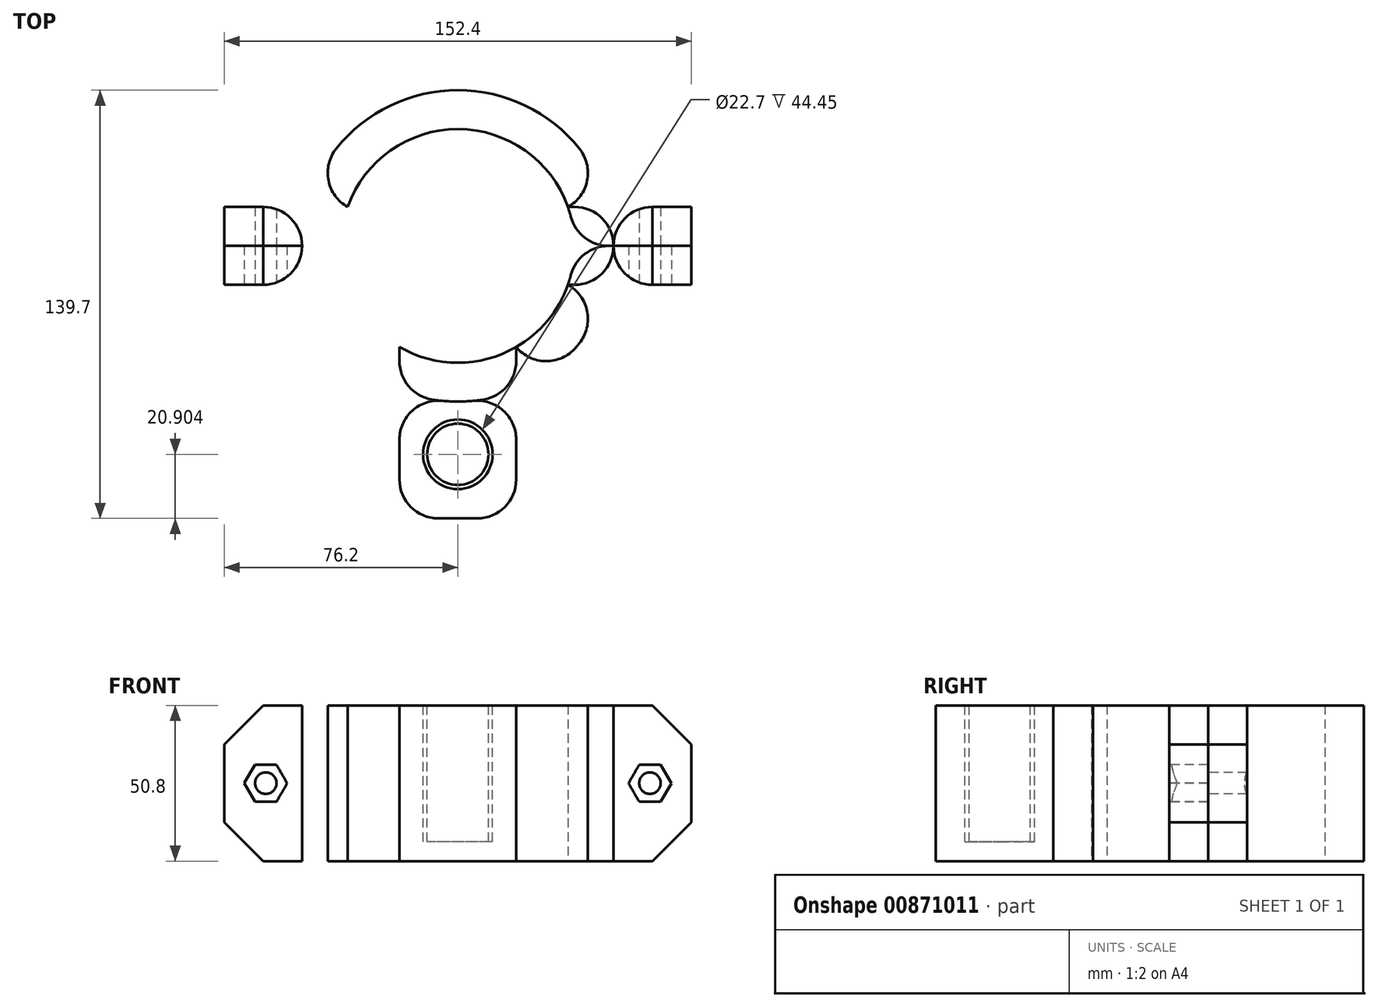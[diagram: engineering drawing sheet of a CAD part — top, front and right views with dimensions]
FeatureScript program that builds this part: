
annotation { "Feature Type Name" : "Feature", "Feature Type Description" : "" }
export const myFeature = defineFeature(function(context is Context, id is Id, definition is map)
    precondition{}
    {
        {
            var Q0;
            Q0=qCreatedBy(makeId("Top.planeOp"),FACE);
            var sketch = newSketch(context, id + "F0", { "sketchPlane" : qUnion([Q0])});
            skCircle(sketch, "E0", {"center": v(0, 0) * mm, "radius": 38.1 * mm});
            skCircle(sketch, "E1", {"center": v(0, 0) * mm, "radius": 50.8 * mm});
            skLineSegment(sketch, "E2.bottom", {"start": v(76.2, -12.7) * mm, "end": v(-76.2, -12.7) * mm});
            skLineSegment(sketch, "E2.top", {"start": v(76.2, 12.7) * mm, "end": v(-76.2, 12.7) * mm});
            skLineSegment(sketch, "E2.left", {"start": v(76.2, -12.7) * mm, "end": v(76.2, 12.7) * mm});
            skLineSegment(sketch, "E2.right", {"start": v(-76.2, -12.7) * mm, "end": v(-76.2, 12.7) * mm});
            skPoint(sketch, "E3", {"position": v(0, -50.8) * mm});
            skLineSegment(sketch, "E4.bottom", {"start": v(19.05, -12.7) * mm, "end": v(-19.05, -12.7) * mm});
            skLineSegment(sketch, "E4.top", {"start": v(19.05, -88.9) * mm, "end": v(-19.05, -88.9) * mm});
            skLineSegment(sketch, "E4.left", {"start": v(19.05, -12.7) * mm, "end": v(19.05, -88.9) * mm});
            skLineSegment(sketch, "E4.right", {"start": v(-19.05, -12.7) * mm, "end": v(-19.05, -88.9) * mm});
            skSolve(sketch);
        }
        {
            var Q0;
            {var subQ0=sQuery(id+"F0.wireOp",EDGE,"E2.top");var subQ1=sQuery(id+"F0.wireOp",EDGE,"E0");var subQ2=makeQuery(id+"F0.imprint","INTERSECT",VERTEX,{"disambiguationData":[OD(0.0)],"derivedFrom":[subQ1,subQ0]});Q0=makeQuery(id+"F0.imprint","IMPRINT",FACE,{"disambiguationData":[TD([[makeQuery(id+"F0.imprint","IMPRINT",EDGE,{"disambiguationData":[TD([[subQ2,1.0]])],"derivedFrom":subQ1}),-1.0]])]});}
            var Q1;
            {var subQ5=sQuery(id+"F0.wireOp",EDGE,"E2.right");Q1=makeQuery(id+"F0.imprint","IMPRINT",FACE,{"disambiguationData":[TD([[makeQuery(id+"F0.imprint","IMPRINT",EDGE,{"derivedFrom":subQ5}),-1.0]])]});}
            var Q2;
            {var subQ0=sQuery(id+"F0.wireOp",EDGE,"E2.top");var subQ1=sQuery(id+"F0.wireOp",EDGE,"E0");var subQ2=makeQuery(id+"F0.imprint","INTERSECT",VERTEX,{"disambiguationData":[OD(0.0)],"derivedFrom":[subQ1,subQ0]});Q2=makeQuery(id+"F0.imprint","IMPRINT",FACE,{"disambiguationData":[TD([[makeQuery(id+"F0.imprint","IMPRINT",EDGE,{"disambiguationData":[TD([[subQ2,-1.0]])],"derivedFrom":subQ1}),-1.0]])]});}
            var Q3;
            {var subQ0=sQuery(id+"F0.wireOp",EDGE,"E2.top");var subQ1=sQuery(id+"F0.wireOp",EDGE,"E0");var subQ2=makeQuery(id+"F0.imprint","INTERSECT",VERTEX,{"disambiguationData":[OD(1.0)],"derivedFrom":[subQ1,subQ0]});Q3=makeQuery(id+"F0.imprint","IMPRINT",FACE,{"disambiguationData":[TD([[makeQuery(id+"F0.imprint","IMPRINT",EDGE,{"disambiguationData":[TD([[subQ2,1.0]])],"derivedFrom":subQ1}),-1.0]])]});}
            var Q4;
            {var subQ5=sQuery(id+"F0.wireOp",EDGE,"E2.left");Q4=makeQuery(id+"F0.imprint","IMPRINT",FACE,{"disambiguationData":[TD([[makeQuery(id+"F0.imprint","IMPRINT",EDGE,{"derivedFrom":subQ5}),1.0]])]});}
            var Q5;
            {var subQ0=sQuery(id+"F0.wireOp",EDGE,"E2.bottom");var subQ1=sQuery(id+"F0.wireOp",EDGE,"E0");var subQ2=makeQuery(id+"F0.imprint","INTERSECT",VERTEX,{"disambiguationData":[OD(0.0)],"derivedFrom":[subQ1,subQ0]});Q5=makeQuery(id+"F0.imprint","IMPRINT",FACE,{"disambiguationData":[TD([[makeQuery(id+"F0.imprint","IMPRINT",EDGE,{"disambiguationData":[TD([[subQ2,-1.0]])],"derivedFrom":subQ1}),-1.0]])]});}
            var Q6;
            {var subQ0=sQuery(id+"F0.wireOp",EDGE,"E4.left");var subQ1=sQuery(id+"F0.wireOp",EDGE,"E0");var subQ2=makeQuery(id+"F0.imprint","INTERSECT",VERTEX,{"derivedFrom":[subQ1,subQ0]});Q6=makeQuery(id+"F0.imprint","IMPRINT",FACE,{"disambiguationData":[TD([[makeQuery(id+"F0.imprint","IMPRINT",EDGE,{"disambiguationData":[TD([[subQ2,-1.0]])],"derivedFrom":subQ1}),-1.0]])]});}
            var Q7;
            {var subQ0=sQuery(id+"F0.wireOp",EDGE,"E4.right");var subQ1=sQuery(id+"F0.wireOp",EDGE,"E0");var subQ2=makeQuery(id+"F0.imprint","INTERSECT",VERTEX,{"derivedFrom":[subQ1,subQ0]});Q7=makeQuery(id+"F0.imprint","IMPRINT",FACE,{"disambiguationData":[TD([[makeQuery(id+"F0.imprint","IMPRINT",EDGE,{"disambiguationData":[TD([[subQ2,-1.0]])],"derivedFrom":subQ1}),-1.0]])]});}
            var Q8;
            {var subQ5=sQuery(id+"F0.wireOp",EDGE,"E4.top");Q8=makeQuery(id+"F0.imprint","IMPRINT",FACE,{"disambiguationData":[TD([[makeQuery(id+"F0.imprint","IMPRINT",EDGE,{"derivedFrom":subQ5}),-1.0]])]});}
            extrude(context, id + "F1", {"entities" : qUnion([Q0, Q1, Q2, Q3, Q4, Q5, Q6, Q7, Q8]), "depth" : 50.8 * mm, "offsetDistance" : 25 * mm});
        }
        {
            var Q0;
            {var subQ0=sQuery(id+"F0.wireOp",EDGE,"E2.bottom");Q0=makeQuery(id+"F1.opExtrude","SWEPT_FACE",FACE,{"disambiguationData":[OSD([subQ0]),TDD([makeQuery(id+"F0.imprint","IMPRINT",EDGE,{"disambiguationData":[TD([[makeQuery(id+"F0.imprint","INTERSECT",VERTEX,{"derivedFrom":[subQ0,sQuery(id+"F0.wireOp",EDGE,"E2.right")]}),1.0]])],"derivedFrom":subQ0})])]});}
            var sketch = newSketch(context, id + "F2", { "sketchPlane" : qUnion([Q0])});
            skPoint(sketch, "E5", {"position": v(-62.7, 25.4) * mm});
            skPoint(sketch, "E5.positionSnap0", {"position": v(-76.2, 25.4) * mm});
            skPoint(sketch, "E5.positionSnap1", {"position": v(-62.7, 50.8) * mm});
            skPoint(sketch, "E6", {"position": v(62.7, 25.4) * mm});
            skCircle(sketch, "E7.cCircle", {"center": v(-62.7, 25.4) * mm, "radius": 7 * mm, "construction": true});
            skLineSegment(sketch, "E7.0", {"start": v(-59.16, 31.44) * mm, "end": v(-55.7, 25.36) * mm});
            skLineSegment(sketch, "E7.1", {"start": v(-55.7, 25.36) * mm, "end": v(-59.23, 19.32) * mm});
            skLineSegment(sketch, "E7.2", {"start": v(-59.23, 19.32) * mm, "end": v(-66.23, 19.36) * mm});
            skLineSegment(sketch, "E7.3", {"start": v(-66.23, 19.36) * mm, "end": v(-69.7, 25.44) * mm});
            skLineSegment(sketch, "E7.4", {"start": v(-69.7, 25.44) * mm, "end": v(-66.16, 31.48) * mm});
            skLineSegment(sketch, "E7.5", {"start": v(-66.16, 31.48) * mm, "end": v(-59.16, 31.44) * mm});
            skCircle(sketch, "E8.cCircle", {"center": v(62.7, 25.4) * mm, "radius": 7 * mm, "construction": true});
            skLineSegment(sketch, "E8.0", {"start": v(55.7, 25.4) * mm, "end": v(59.2, 31.46) * mm});
            skLineSegment(sketch, "E8.1", {"start": v(59.2, 31.46) * mm, "end": v(66.2, 31.46) * mm});
            skLineSegment(sketch, "E8.2", {"start": v(66.2, 31.46) * mm, "end": v(69.7, 25.4) * mm});
            skLineSegment(sketch, "E8.3", {"start": v(69.7, 25.4) * mm, "end": v(66.2, 19.34) * mm});
            skLineSegment(sketch, "E8.4", {"start": v(66.2, 19.34) * mm, "end": v(59.2, 19.34) * mm});
            skLineSegment(sketch, "E8.5", {"start": v(59.2, 19.34) * mm, "end": v(55.7, 25.4) * mm});
            skSolve(sketch);
        }
        {
            var Q0;
            Q0 = qSketchRegion(id + "F2", true);
            extrude(context, id + "F3", {"entities" : qUnion([Q0]), "operationType" : NewBodyOperationType.REMOVE, "oppositeDirection" : true, "depth" : 12.7 * mm, "offsetDistance" : 25 * mm});
        }
        {
            var Q0;
            Q0=makeQuery(id+"F1.opExtrude","CAP_EDGE",EDGE,{"disambiguationData":[OSD([sQuery(id+"F0.wireOp",EDGE,"E2.right")])],"isStart":false});
            var Q1;
            Q1=makeQuery(id+"F1.opExtrude","CAP_EDGE",EDGE,{"disambiguationData":[OSD([sQuery(id+"F0.wireOp",EDGE,"E2.right")])],"isStart":true});
            var Q2;
            Q2=makeQuery(id+"F1.opExtrude","CAP_EDGE",EDGE,{"disambiguationData":[OSD([sQuery(id+"F0.wireOp",EDGE,"E2.left")])],"isStart":false});
            var Q3;
            Q3=makeQuery(id+"F1.opExtrude","CAP_EDGE",EDGE,{"disambiguationData":[OSD([sQuery(id+"F0.wireOp",EDGE,"E2.left")])],"isStart":true});
            chamfer(context, id + "F4", {"entities" : qUnion([Q0, Q1, Q2, Q3]), "width" : 12.7 * mm, "tangentPropagation" : true});
        }
        {
            var Q0;
            Q0=makeQuery(id+"F1.opExtrude","CAP_FACE",FACE,{"disambiguationData":[OSD([sQuery(id+"F0.wireOp",EDGE,"E0"),sQuery(id+"F0.wireOp",EDGE,"E1"),sQuery(id+"F0.wireOp",EDGE,"E2.bottom"),sQuery(id+"F0.wireOp",EDGE,"E2.top"),sQuery(id+"F0.wireOp",EDGE,"E2.left"),sQuery(id+"F0.wireOp",EDGE,"E2.right"),sQuery(id+"F0.wireOp",EDGE,"E4.top"),sQuery(id+"F0.wireOp",EDGE,"E4.left"),sQuery(id+"F0.wireOp",EDGE,"E4.right")])],"isStart":false});
            var sketch = newSketch(context, id + "F5", { "sketchPlane" : qUnion([Q0])});
            skPoint(sketch, "E9", {"position": v(0, -68) * mm});
            skPoint(sketch, "E9.positionSnap0", {"position": v(-19.05, -68) * mm});
            skPoint(sketch, "E9.positionSnap1", {"position": v(0, -88.9) * mm});
            skCircle(sketch, "E10", {"center": v(0, -68) * mm, "radius": 11.35 * mm});
            skCircle(sketch, "E11", {"center": v(0, -68) * mm, "radius": 10 * mm});
            skSolve(sketch);
        }
        {
            var Q0;
            Q0=makeQuery(id+"F5.imprint","IMPRINT",FACE,{"disambiguationData":[TD([[makeQuery(id+"F5.imprint","IMPRINT",EDGE,{"derivedFrom":sQuery(id+"F5.wireOp",EDGE,"E10")}),1.0]])]});
            var Q1;
            Q1=sQuery(id+"F5.wireOp",EDGE,"E11");
            var Q2;
            Q2=sQuery(id+"F5.wireOp",EDGE,"E10");
            extrude(context, id + "F6", {"entities" : qUnion([Q0]), "operationType" : NewBodyOperationType.REMOVE, "surfaceEntities" : qUnion([Q1, Q2]), "oppositeDirection" : true, "depth" : 44.45 * mm, "offsetDistance" : 25 * mm});
        }
        {
            var Q0;
            Q0=makeQuery(id+"F1.opExtrude","SWEPT_EDGE",EDGE,{"disambiguationData":[OSD([sQuery(id+"F0.wireOp",EDGE,"E4.top"),sQuery(id+"F0.wireOp",EDGE,"E4.right")])]});
            var Q1;
            Q1=makeQuery(id+"F1.opExtrude","SWEPT_EDGE",EDGE,{"disambiguationData":[OSD([sQuery(id+"F0.wireOp",EDGE,"E4.top"),sQuery(id+"F0.wireOp",EDGE,"E4.left")])]});
            var Q2;
            Q2=makeQuery(id+"F1.opExtrude","SWEPT_EDGE",EDGE,{"disambiguationData":[OSD([sQuery(id+"F0.wireOp",EDGE,"E1"),sQuery(id+"F0.wireOp",EDGE,"E4.right")])]});
            var Q3;
            Q3=makeQuery(id+"F1.opExtrude","SWEPT_EDGE",EDGE,{"disambiguationData":[OSD([sQuery(id+"F0.wireOp",EDGE,"E1"),sQuery(id+"F0.wireOp",EDGE,"E4.left")])]});
            var Q4;
            {var subQ0=sQuery(id+"F0.wireOp",EDGE,"E2.bottom");var subQ1=sQuery(id+"F0.wireOp",EDGE,"E1");Q4=makeQuery(id+"F1.opExtrude","SWEPT_EDGE",EDGE,{"disambiguationData":[OSD([subQ1,subQ0]),TDD([makeQuery(id+"F0.imprint","INTERSECT",VERTEX,{"disambiguationData":[OD(1.0)],"derivedFrom":[subQ1,subQ0]})])]});}
            var Q5;
            {var subQ0=sQuery(id+"F0.wireOp",EDGE,"E2.bottom");var subQ1=sQuery(id+"F0.wireOp",EDGE,"E1");Q5=makeQuery(id+"F1.opExtrude","SWEPT_EDGE",EDGE,{"disambiguationData":[OSD([subQ1,subQ0]),TDD([makeQuery(id+"F0.imprint","INTERSECT",VERTEX,{"disambiguationData":[OD(0.0)],"derivedFrom":[subQ1,subQ0]})])]});}
            var Q6;
            {var subQ0=sQuery(id+"F0.wireOp",EDGE,"E2.top");var subQ1=sQuery(id+"F0.wireOp",EDGE,"E1");Q6=makeQuery(id+"F1.opExtrude","SWEPT_EDGE",EDGE,{"disambiguationData":[OSD([subQ1,subQ0]),TDD([makeQuery(id+"F0.imprint","INTERSECT",VERTEX,{"disambiguationData":[OD(1.0)],"derivedFrom":[subQ1,subQ0]})])]});}
            var Q7;
            {var subQ0=sQuery(id+"F0.wireOp",EDGE,"E2.top");var subQ1=sQuery(id+"F0.wireOp",EDGE,"E1");Q7=makeQuery(id+"F1.opExtrude","SWEPT_EDGE",EDGE,{"disambiguationData":[OSD([subQ1,subQ0]),TDD([makeQuery(id+"F0.imprint","INTERSECT",VERTEX,{"disambiguationData":[OD(0.0)],"derivedFrom":[subQ1,subQ0]})])]});}
            fillet(context, id + "F7", {"entities" : qUnion([Q0, Q1, Q2, Q3, Q4, Q5, Q6, Q7]), "radius" : 12.7 * mm, "tangentPropagation" : true, "allowEdgeOverflow" : false});
        }
        {
            var Q0;
            Q0=makeQuery(id+"F3.boolean.opBoolean","COPY",FACE,{"derivedFrom":makeQuery(id+"F3.opExtrude","CAP_FACE",FACE,{"disambiguationData":[OSD([sQuery(id+"F2.wireOp",EDGE,"E7.0"),sQuery(id+"F2.wireOp",EDGE,"E7.1"),sQuery(id+"F2.wireOp",EDGE,"E7.2"),sQuery(id+"F2.wireOp",EDGE,"E7.3"),sQuery(id+"F2.wireOp",EDGE,"E7.4"),sQuery(id+"F2.wireOp",EDGE,"E7.5")])],"isStart":false})});
            var sketch = newSketch(context, id + "F8", { "sketchPlane" : qUnion([Q0])});
            skPoint(sketch, "E12", {"position": v(-62.66, 25.44) * mm});
            skPoint(sketch, "E12.positionSnap0", {"position": v(-62.66, 31.46) * mm});
            skPoint(sketch, "E13", {"position": v(62.7, 25.44) * mm});
            skPoint(sketch, "E14", {"position": v(62.7, 31.46) * mm});
            skCircle(sketch, "E15", {"center": v(-62.66, 25.44) * mm, "radius": 3.5 * mm});
            skCircle(sketch, "E16", {"center": v(62.7, 25.44) * mm, "radius": 3.5 * mm});
            skSolve(sketch);
        }
        {
            var Q0;
            Q0=makeQuery(id+"F8.imprint","IMPRINT",FACE,{"disambiguationData":[TD([[makeQuery(id+"F8.imprint","IMPRINT",EDGE,{"derivedFrom":sQuery(id+"F8.wireOp",EDGE,"E15")}),1.0]])]});
            var Q1;
            Q1=makeQuery(id+"F8.imprint","IMPRINT",FACE,{"disambiguationData":[TD([[makeQuery(id+"F8.imprint","IMPRINT",EDGE,{"derivedFrom":sQuery(id+"F8.wireOp",EDGE,"E16")}),1.0]])]});
            extrude(context, id + "F9", {"entities" : qUnion([Q0, Q1]), "operationType" : NewBodyOperationType.REMOVE, "endBound" : BoundingType.THROUGH_ALL, "oppositeDirection" : true, "depth" : 25 * mm, "offsetDistance" : 25 * mm});
        }
        {
            var Q0;
            Q0=qCreatedBy(makeId("Front.planeOp"),FACE);
            var sketch = newSketch(context, id + "F10", { "sketchPlane" : qUnion([Q0])});
            skLineSegment(sketch, "E17.bottom", {"start": v(-97.94, 76.17) * mm, "end": v(85.9, 76.17) * mm});
            skLineSegment(sketch, "E17.top", {"start": v(-97.94, -81.22) * mm, "end": v(85.9, -81.22) * mm});
            skLineSegment(sketch, "E17.left", {"start": v(-97.94, 76.17) * mm, "end": v(-97.94, -81.22) * mm});
            skLineSegment(sketch, "E17.right", {"start": v(85.9, 76.17) * mm, "end": v(85.9, -81.22) * mm});
            skSolve(sketch);
        }
        {
            var Q0;
            Q0 = qSketchRegion(id + "F10", true);
            extrude(context, id + "F11", {"entities" : qUnion([Q0]), "operationType" : NewBodyOperationType.REMOVE, "depth" : 0 * mm, "offsetDistance" : 25 * mm});
        }
        {
            var Q0;
            Q0=makeQuery(id+"F11.boolean.opBoolean","INTERSECT",EDGE,{"disambiguationData":[OD(0.0)],"derivedFrom":[makeQuery(id+"F1.opExtrude","SWEPT_FACE",FACE,{"disambiguationData":[OSD([sQuery(id+"F0.wireOp",EDGE,"E0")])]}),makeQuery(id+"F11.opExtrude","CAP_FACE",FACE,{"disambiguationData":[OSD([sQuery(id+"F10.wireOp",EDGE,"E17.bottom"),sQuery(id+"F10.wireOp",EDGE,"E17.top"),sQuery(id+"F10.wireOp",EDGE,"E17.left"),sQuery(id+"F10.wireOp",EDGE,"E17.right")])],"isStart":false})]});
            var Q1;
            {var subQ0=makeQuery(id+"F1.opExtrude","SWEPT_FACE",FACE,{"disambiguationData":[OSD([sQuery(id+"F0.wireOp",EDGE,"E0")])]});var subQ1=makeQuery(id+"F11.opExtrude","CAP_FACE",FACE,{"disambiguationData":[OSD([sQuery(id+"F10.wireOp",EDGE,"E17.bottom"),sQuery(id+"F10.wireOp",EDGE,"E17.top"),sQuery(id+"F10.wireOp",EDGE,"E17.left"),sQuery(id+"F10.wireOp",EDGE,"E17.right")])],"isStart":true});Q1=makeQuery(id+"F11.boolean.opBoolean","INTERSECT",EDGE,{"disambiguationData":[topologyDisambiguationEdgeConnected([makeQuery(id+"F3.boolean.opBoolean","COPY",FACE,{"derivedFrom":makeQuery(id+"F3.opExtrude","CAP_FACE",FACE,{"disambiguationData":[OSD([sQuery(id+"F2.wireOp",EDGE,"E7.0"),sQuery(id+"F2.wireOp",EDGE,"E7.1"),sQuery(id+"F2.wireOp",EDGE,"E7.2"),sQuery(id+"F2.wireOp",EDGE,"E7.3"),sQuery(id+"F2.wireOp",EDGE,"E7.4"),sQuery(id+"F2.wireOp",EDGE,"E7.5")])],"isStart":false})})])],"derivedFrom":[subQ0,subQ1]});}
            var Q2;
            {var subQ0=makeQuery(id+"F1.opExtrude","SWEPT_FACE",FACE,{"disambiguationData":[OSD([sQuery(id+"F0.wireOp",EDGE,"E0")])]});var subQ1=makeQuery(id+"F11.opExtrude","CAP_FACE",FACE,{"disambiguationData":[OSD([sQuery(id+"F10.wireOp",EDGE,"E17.bottom"),sQuery(id+"F10.wireOp",EDGE,"E17.top"),sQuery(id+"F10.wireOp",EDGE,"E17.left"),sQuery(id+"F10.wireOp",EDGE,"E17.right")])],"isStart":true});Q2=makeQuery(id+"F11.boolean.opBoolean","INTERSECT",EDGE,{"disambiguationData":[topologyDisambiguationEdgeConnected([makeQuery(id+"F3.boolean.opBoolean","COPY",FACE,{"derivedFrom":makeQuery(id+"F3.opExtrude","CAP_FACE",FACE,{"disambiguationData":[OSD([sQuery(id+"F2.wireOp",EDGE,"E8.0"),sQuery(id+"F2.wireOp",EDGE,"E8.1"),sQuery(id+"F2.wireOp",EDGE,"E8.2"),sQuery(id+"F2.wireOp",EDGE,"E8.3"),sQuery(id+"F2.wireOp",EDGE,"E8.4"),sQuery(id+"F2.wireOp",EDGE,"E8.5")])],"isStart":false})})])],"derivedFrom":[subQ0,subQ1]});}
            var Q3;
            Q3=makeQuery(id+"F11.boolean.opBoolean","INTERSECT",EDGE,{"disambiguationData":[OD(1.0)],"derivedFrom":[makeQuery(id+"F1.opExtrude","SWEPT_FACE",FACE,{"disambiguationData":[OSD([sQuery(id+"F0.wireOp",EDGE,"E0")])]}),makeQuery(id+"F11.opExtrude","CAP_FACE",FACE,{"disambiguationData":[OSD([sQuery(id+"F10.wireOp",EDGE,"E17.bottom"),sQuery(id+"F10.wireOp",EDGE,"E17.top"),sQuery(id+"F10.wireOp",EDGE,"E17.left"),sQuery(id+"F10.wireOp",EDGE,"E17.right")])],"isStart":false})]});
            fillet(context, id + "F12", {"entities" : qUnion([Q0, Q1, Q2, Q3]), "radius" : 12.7 * mm, "tangentPropagation" : true, "allowEdgeOverflow" : false});
        }
    });
